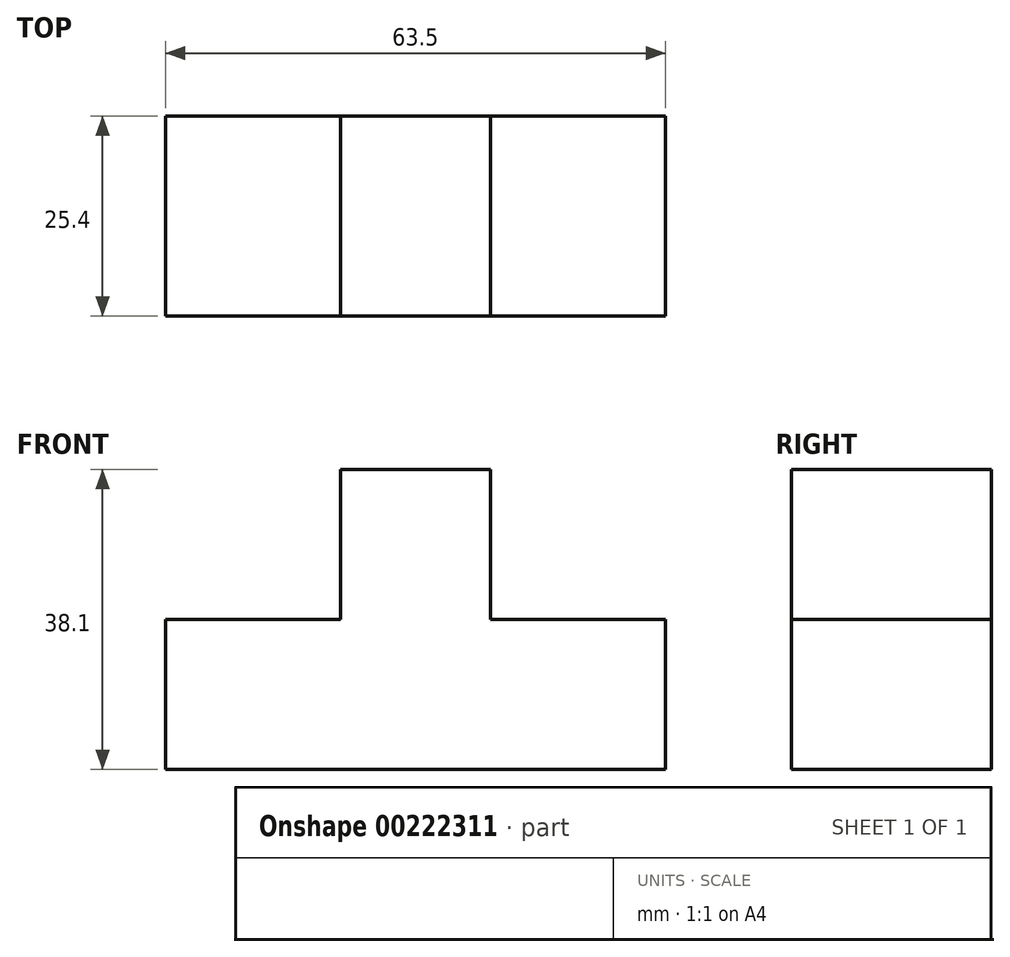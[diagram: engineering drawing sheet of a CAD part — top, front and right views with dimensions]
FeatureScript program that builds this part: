
annotation { "Feature Type Name" : "Feature", "Feature Type Description" : "" }
export const myFeature = defineFeature(function(context is Context, id is Id, definition is map)
    precondition{}
    {
        {
            var Q0;
            Q0=qCreatedBy(makeId("Front.planeOp"),FACE);
            var sketch = newSketch(context, id + "F0", { "sketchPlane" : qUnion([Q0])});
            skLineSegment(sketch, "E0.bottom", {"start": v(-41.28, 16.62) * mm, "end": v(22.23, 16.62) * mm});
            skLineSegment(sketch, "E0.top", {"start": v(-41.28, 35.67) * mm, "end": v(22.23, 35.67) * mm});
            skLineSegment(sketch, "E0.left", {"start": v(-41.28, 16.62) * mm, "end": v(-41.28, 35.67) * mm});
            skLineSegment(sketch, "E0.right", {"start": v(22.22, 16.62) * mm, "end": v(22.22, 35.67) * mm});
            skPoint(sketch, "E0.middle", {"position": v(-9.53, 26.14) * mm});
            skLineSegment(sketch, "E1.bottom", {"start": v(0, 35.67) * mm, "end": v(-19.05, 35.67) * mm});
            skLineSegment(sketch, "E1.top", {"start": v(0, 54.72) * mm, "end": v(-19.05, 54.72) * mm});
            skLineSegment(sketch, "E1.left", {"start": v(0, 35.67) * mm, "end": v(0, 54.72) * mm});
            skLineSegment(sketch, "E1.right", {"start": v(-19.05, 35.67) * mm, "end": v(-19.05, 54.72) * mm});
            skPoint(sketch, "E1.middle", {"position": v(-9.53, 45.2) * mm});
            skPoint(sketch, "E1.middle.positionSnap0", {"position": v(-9.53, 35.67) * mm});
            skPoint(sketch, "E1.centerSnap0", {"position": v(-9.53, 35.67) * mm});
            skSolve(sketch);
        }
        {
            var Q0;
            Q0=qSketchRegion(id+"F0",true);
            extrude(context, id + "F1", {"entities" : qUnion([Q0]), "endBound" : BoundingType.SYMMETRIC, "depth" : 25.4 * mm});
        }
    });
